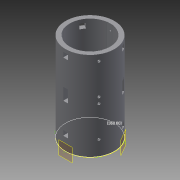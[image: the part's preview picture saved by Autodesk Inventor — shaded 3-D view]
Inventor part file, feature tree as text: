
AUTODESK INVENTOR PART (.ipt)
format: ipt  version: 2013 (Build 170138000, 138)  size: 256,000 bytes
history: native  units: mm
features: sketch x6, other x5, extrude x3, pattern_circular x3, hole x2
ambient origin geometry x8: Origin, YZ Plane, XZ Plane, XY Plane, X Axis, Y Axis, Z Axis, Center Point
feature tree (19):
  other  "ソリッド1"
  extrude  "押し出し1"  Depth=26.0mm
  extrude  "押し出し2"  Depth=20.0mm
  hole  "穴1"  [1 undecoded]
  pattern_circular  "円形状パターン1"  [2 undecoded]
  sketch  "スケッチ4"
  other  "作業平面1"
  other  "作業平面3"
  other  "作業平面7"
  extrude  "押し出し3"  Depth=10.8mm
  pattern_circular  "円形状パターン2"  [2 undecoded]
  other  "作業平面8"
  hole  "穴2"  [1 undecoded]
  pattern_circular  "円形状パターン3"  Count=3 Angle=360.0deg
  sketch  "スケッチ1"
  sketch  "スケッチ2"
  sketch  "スケッチ3"
  sketch  "スケッチ5"
  sketch  "スケッチ6"
note: 6 required parameter values undecoded (feature->parameter linkage not recoverable at this tier; creation-order binding heuristic only, values carry confidence <= 0.55)
